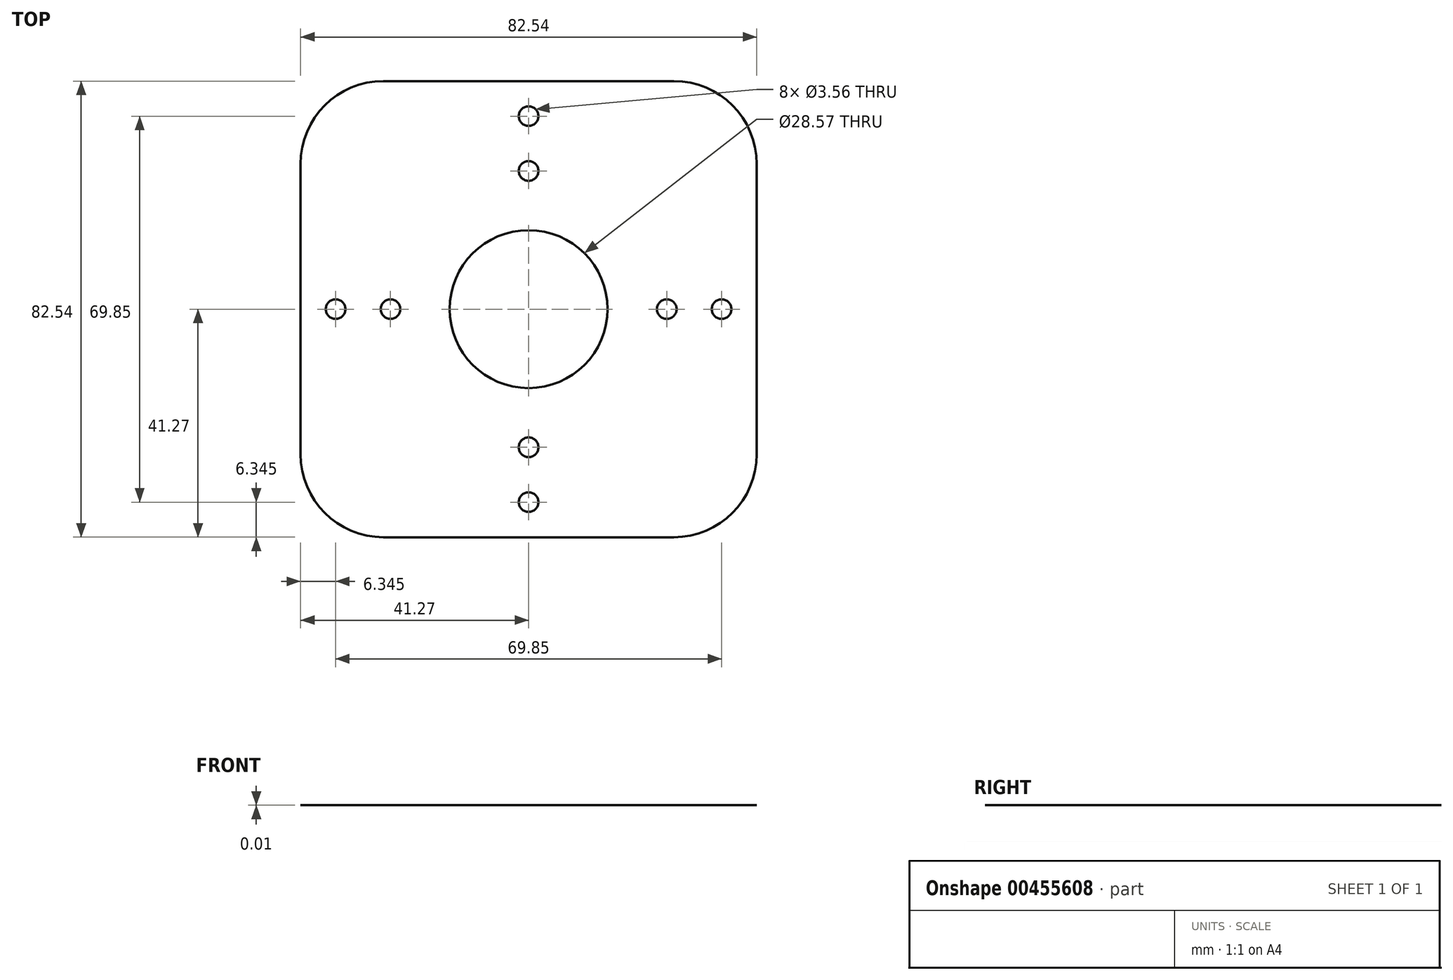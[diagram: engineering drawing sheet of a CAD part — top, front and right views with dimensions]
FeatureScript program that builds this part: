
annotation { "Feature Type Name" : "Feature", "Feature Type Description" : "" }
export const myFeature = defineFeature(function(context is Context, id is Id, definition is map)
    precondition{}
    {
        {
            var Q0;
            Q0=qCreatedBy(makeId("Top.planeOp"),FACE);
            var sketch = newSketch(context, id + "F0", { "sketchPlane" : qUnion([Q0])});
            skLineSegment(sketch, "E0.bottom", {"start": v(41.28, 41.27) * mm, "end": v(-41.28, 41.28) * mm});
            skLineSegment(sketch, "E0.top", {"start": v(41.28, -41.28) * mm, "end": v(-41.28, -41.28) * mm});
            skLineSegment(sketch, "E0.left", {"start": v(41.28, 41.27) * mm, "end": v(41.28, -41.28) * mm});
            skLineSegment(sketch, "E0.right", {"start": v(-41.28, 41.28) * mm, "end": v(-41.28, -41.27) * mm});
            skPoint(sketch, "E0.middle", {"position": v(0, 0) * mm});
            skCircle(sketch, "E1", {"center": v(0, 34.93) * mm, "radius": 1.78 * mm});
            skCircle(sketch, "E2", {"center": v(0, 0) * mm, "radius": 14.29 * mm});
            skCircle(sketch, "E3", {"center": v(0, 25) * mm, "radius": 1.78 * mm});
            skCircle(sketch, "E4.1.0", {"center": v(-34.93, 0) * mm, "radius": 1.78 * mm});
            skCircle(sketch, "E4.1.1", {"center": v(-25, 0) * mm, "radius": 1.78 * mm});
            skCircle(sketch, "E4.2.0", {"center": v(0, -34.93) * mm, "radius": 1.78 * mm});
            skCircle(sketch, "E4.2.1", {"center": v(0, -25) * mm, "radius": 1.78 * mm});
            skCircle(sketch, "E4.3.0", {"center": v(34.93, 0) * mm, "radius": 1.78 * mm});
            skCircle(sketch, "E4.3.1", {"center": v(25, 0) * mm, "radius": 1.78 * mm});
            skSolve(sketch);
        }
        {
            var Q0;
            Q0=makeQuery(id+"F0.imprint","IMPRINT",FACE,{"disambiguationData":[TD([[makeQuery(id+"F0.imprint","IMPRINT",EDGE,{"derivedFrom":sQuery(id+"F0.wireOp",EDGE,"E0.bottom")}),1.0]])]});
            extrude(context, id + "F1", {"entities" : qUnion([Q0]), "depth" : 1 / 101.6 * mm});
        }
        {
            var Q0;
            Q0=makeQuery(id+"F1.opExtrude","SWEPT_EDGE",EDGE,{"disambiguationData":[OSD([sQuery(id+"F0.wireOp",EDGE,"E0.bottom"),sQuery(id+"F0.wireOp",EDGE,"E0.right")])]});
            var Q1;
            Q1=makeQuery(id+"F1.opExtrude","SWEPT_EDGE",EDGE,{"disambiguationData":[OSD([sQuery(id+"F0.wireOp",EDGE,"E0.top"),sQuery(id+"F0.wireOp",EDGE,"E0.right")])]});
            var Q2;
            Q2=makeQuery(id+"F1.opExtrude","SWEPT_EDGE",EDGE,{"disambiguationData":[OSD([sQuery(id+"F0.wireOp",EDGE,"E0.bottom"),sQuery(id+"F0.wireOp",EDGE,"E0.left")])]});
            var Q3;
            Q3=makeQuery(id+"F1.opExtrude","SWEPT_EDGE",EDGE,{"disambiguationData":[OSD([sQuery(id+"F0.wireOp",EDGE,"E0.top"),sQuery(id+"F0.wireOp",EDGE,"E0.left")])]});
            fillet(context, id + "F2", {"entities" : qUnion([Q0, Q1, Q2, Q3]), "radius" : 15 * mm, "tangentPropagation" : true, "allowEdgeOverflow" : false});
        }
    });
